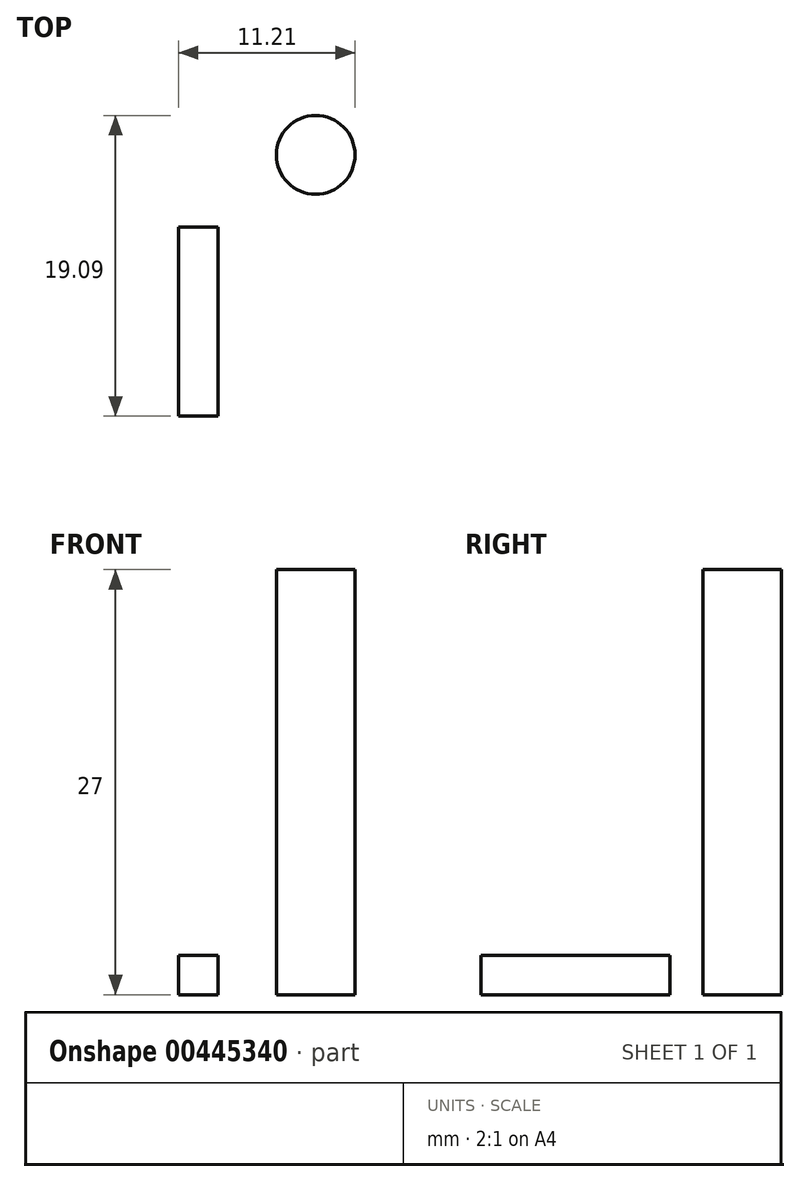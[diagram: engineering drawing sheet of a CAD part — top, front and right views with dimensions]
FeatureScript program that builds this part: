
annotation { "Feature Type Name" : "Feature", "Feature Type Description" : "" }
export const myFeature = defineFeature(function(context is Context, id is Id, definition is map)
    precondition{}
    {
        {
            var Q0;
            Q0=qCreatedBy(makeId("Top.planeOp"),FACE);
            var sketch = newSketch(context, id + "F0", { "sketchPlane" : qUnion([Q0])});
            skCircle(sketch, "E0", {"center": v(61.1, -22.5) * mm, "radius": 23.3 * mm});
            skCircle(sketch, "E1", {"center": v(49.04, -21.25) * mm, "radius": 1.46 * mm});
            skCircle(sketch, "E2", {"center": v(48.63, -19.84) * mm, "radius": 1.46 * mm});
            skCircle(sketch, "E3", {"center": v(22.25, -45.2) * mm, "radius": 2.5 * mm});
            skSolve(sketch);
        }
        {
            var Q0;
            Q0=makeQuery(id+"F0.imprint","IMPRINT",FACE,{"disambiguationData":[TD([[makeQuery(id+"F0.imprint","IMPRINT",EDGE,{"derivedFrom":sQuery(id+"F0.wireOp",EDGE,"E3")}),1.0]])]});
            extrude(context, id + "F1", {"entities" : qUnion([Q0]), "depth" : 27 * mm});
        }
        {
            var Q0;
            Q0=qCreatedBy(makeId("Top.planeOp"),FACE);
            var sketch = newSketch(context, id + "F2", { "sketchPlane" : qUnion([Q0])});
            skLineSegment(sketch, "E4.bottom", {"start": v(13.54, -49.8) * mm, "end": v(16.04, -49.8) * mm});
            skLineSegment(sketch, "E4.top", {"start": v(13.54, -61.8) * mm, "end": v(16.04, -61.8) * mm});
            skLineSegment(sketch, "E4.left", {"start": v(13.54, -49.8) * mm, "end": v(13.54, -61.8) * mm});
            skLineSegment(sketch, "E4.right", {"start": v(16.04, -49.8) * mm, "end": v(16.04, -61.8) * mm});
            skSolve(sketch);
        }
        {
            var Q0;
            Q0 = qSketchRegion(id + "F2", true);
            extrude(context, id + "F3", {"entities" : qUnion([Q0]), "depth" : 2.5 * mm});
        }
    });
